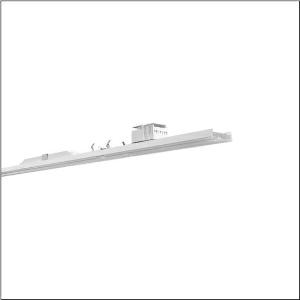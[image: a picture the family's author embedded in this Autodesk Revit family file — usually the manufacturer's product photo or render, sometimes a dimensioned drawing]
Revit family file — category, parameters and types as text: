
# Revit family: licross_r__21_recessed_mo_52tl14dne7xf_5002
name_source: partatom
category: Lighting Fixtures
units: mm (PartAtom-declared; Revit-internal decimal feet)

## family parameters
Cut with Voids When Loaded = No
Host = Face
Light Source = No
Part Type = Normal
Room Calculation Point = No
Round Connector Dimension = Use Diameter
Shared = No

## types (1)
- --- (1 x LED, 7340 lm, 61.1 W, 5000K)
    Apparent Load = 61 VA
    CIE Flux Codes = 56 84 97 100 100
    Color Rendering = 90
    Color Temperature = 5000K
    Default Elevation = 1800 mm
    Description = Licross® 21 Recessed MO, luminaire insert, of sheet steel, galvanised, coil coated, white, length: 1.500mm, width: 66mm, height: 67mm, LED rated luminous flux: 7.340lm, light colour: 950, control gear: DALI 2, control gear: ECG DALI, with plug, 5-pole, with phase selection, mains connection: 220..240V, AC, 50/60Hz, rated input power: 61W, halogen-free wiring, primary optical cover: cover, of PMMA, light emission: direct distribution, primary light characteristic: asymmetric, protection rating (complete): IP40, insulation class (complete): insulation class I (protective earthing), certification: CE, ENEC, VDE, UKCA, protection symbol: D if used in an environment without relevant dust loads with corresponding accessories, impact resistance: IK06, permissible ambient temperature for indoor applications: -25..+35°C, corresponds to IFS (International Featured Standards) requirements for safety and quality in the food industry, reducing of maximum allowable ambient temperature of 5°C with ceiling mounting, LABS conformity tested according to VDMA 24364:2018-05, packaging unit: 1 piece
    Height = 58 mm
    Lamp = 1 x LED
    Lamp Light Flux = 7340 lm
    Lamp Power = 61.1 W
    Lamp count = 1
    Length = 1500 mm
    Luminous efficacy = 120 lm/W
    Manufacturer = Siteco
    ModVariant = No
    Model = 52TL14DNE7XF
    Mounting Place = Ceiling
    Mounting Type = Pendant
    Number of Poles = 1
    OnlyDefault = Yes
    Power Factor = 1
    Product Name = Licross® 21 Recessed MO
    Product group = luminaire insert
    ProductGroupID = 901
    Protection Class = Protection class I
    Protection Degree = IP 40
    RLX_Detail_Level = 1
    RLX_Emergency_Light_Flux = 0 lm
    RLX_Emergency_Type = 0
    RLX_Emergency_Type_DB = No
    RlxData = <blob elided: 22977 chars, md5=69f0efbe>
    Socket = socket
    Standby Power = 0 W
    System Light Flux = 7340 lm
    System Power = 61 W
    Type Comments = factory setting: luminous flux: 100 % | dim-lin: 254 | 405 mA
    Type Image = l_1296935.jpg
    URL = http://relux.com
    VarID = @adj_136233
    Voltage = 0 V
    Weight = 0.00 kg
    Width = 66 mm

## geometry (parser evidence)
native form markers: Blend x4, Sweep x11
no freeform markers — native parametric forms only
